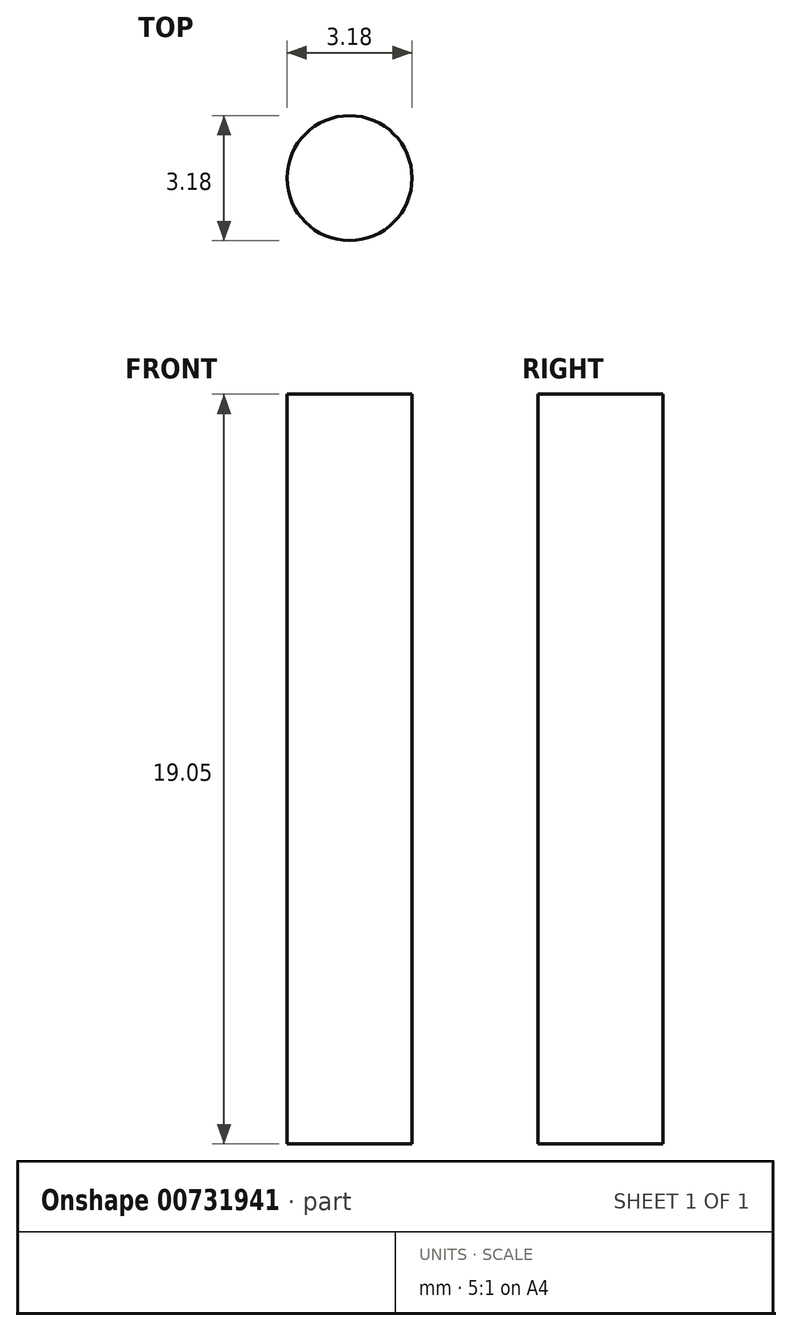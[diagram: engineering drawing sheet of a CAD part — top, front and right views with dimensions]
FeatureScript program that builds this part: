
annotation { "Feature Type Name" : "Feature", "Feature Type Description" : "" }
export const myFeature = defineFeature(function(context is Context, id is Id, definition is map)
    precondition{}
    {
        {
            var Q0;
            Q0=qCreatedBy(makeId("Top.planeOp"),FACE);
            var sketch = newSketch(context, id + "F0", { "sketchPlane" : qUnion([Q0])});
            skCircle(sketch, "E0", {"center": v(0, 0) * mm, "radius": 1.59 * mm});
            skSolve(sketch);
        }
        {
            var Q0;
            Q0=makeQuery(id+"F0.imprint","IMPRINT",FACE,{"disambiguationData":[TD([[makeQuery(id+"F0.imprint","IMPRINT",EDGE,{"derivedFrom":sQuery(id+"F0.wireOp",EDGE,"E0")}),1.0]])]});
            extrude(context, id + "F1", {"entities" : qUnion([Q0]), "depth" : 19.05 * mm, "offsetDistance" : 25.4 * mm});
        }
    });
